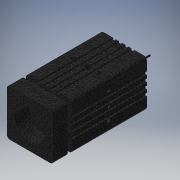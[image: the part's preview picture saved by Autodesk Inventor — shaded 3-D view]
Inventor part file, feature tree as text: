
AUTODESK INVENTOR PART (.ipt)
format: ipt  version: 2019 (Build 230136000, 136)  size: 364,544 bytes
history: native  units: in
note: dims shown in document units (in); Inventor stores cm internally (conversion verified against a paired STEP export)
features: sketch x7, extrude x6, projected_geometry x6, pattern_circular x2, hole x1
ambient origin geometry x8: Origin, YZ Plane, XZ Plane, XY Plane, X Axis, Y Axis, Z Axis, Center Point
bodies: Solid1 (feature_tree)
feature tree (22):
  extrude  "Extrusion1"  Depth=1.1772in
  extrude  "Extrusion2"  Depth=1.8988in TaperAngle=0.0deg
  extrude  "Extrusion3"  Depth=0.2756in TaperAngle=0.0deg
  pattern_circular  "Circular Pattern1"  [2 undecoded]
  hole  "Hole1"  [1 undecoded]
  extrude  "Extrusion4"  Depth=0.3937in
  extrude  "Extrusion5"  Depth=0.3937in
  extrude  "Extrusion7"  Depth=0.3937in TaperAngle=0.0deg
  pattern_circular  "Circular Pattern2"  Count=4 Angle=360.0deg
  sketch  "Sketch1"  dims[d0=1.1772in d1=1.1772in]
  sketch  "Sketch2"  dims[d2=0.0787in d3=1.8988in d4=0.0in]
  projected_geometry  "Projected Loop1"
  sketch  "Sketch3"  dims[d5=0.5in d6=0.2756in d7=0.0in]
  projected_geometry  "Projected Loop2"
  sketch  "Sketch4"  dims[d8=0.0787in]
  projected_geometry  "Projected Loop3"
  projected_geometry  "Projected Loop4"
  sketch  "Sketch5"  dims[d9=0.0394in]
  sketch  "Sketch6"  dims[d10=0.0787in]
  projected_geometry  "Projected Loop5"
  sketch  "Sketch8"  dims[d11=0.0787in d12=0.0787in d13=0.0394in d14=0.0787in d15=0.0787in d16=0.0394in d17=0.0in d18=1.5748in d19=360.0deg d21=0.9646in d22=0.9646in d23=0.2677in d24=0.2677in d25=0.1102in d26=0.2362in d27=0.2362in d28=0.0984in d29=90.0deg d30=0.4724in d31=0.8108in d32=0.8661in d33=0.8661in d34=0.0787in d35=0.0787in d36=0.0787in d37=0.0787in d38=0.1181in d39=0.0in d40=0.0787in d41=0.3701in d42=0.0in d46=0.0394in d47=0.3937in d48=0.0in d49=1.5748in d50=360.0deg]
  projected_geometry  "Projected Loop6"
note: 3 required parameter values undecoded (feature->parameter linkage not recoverable at this tier; creation-order binding heuristic only, values carry confidence <= 0.55)
